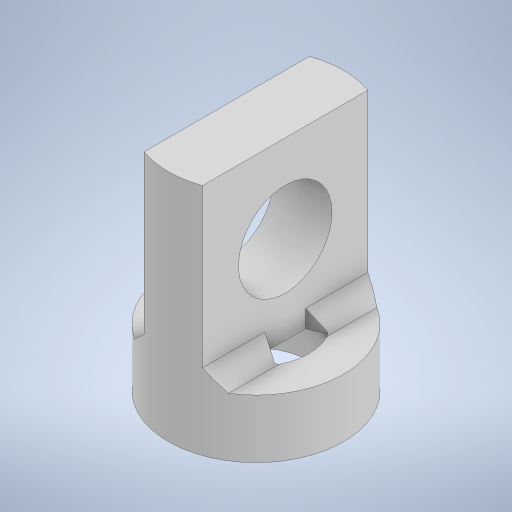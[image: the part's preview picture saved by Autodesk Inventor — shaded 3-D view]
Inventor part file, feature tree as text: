
AUTODESK INVENTOR PART (.ipt)
format: ipt  version: 2024 (Build 280153000, 153)  size: 267,776 bytes
history: native  units: mm
features: extrude x3, sketch x3, chamfer x2, other x1, projected_geometry x1
ambient origin geometry x8: Origin, YZ Plane, XZ Plane, XY Plane, X Axis, Y Axis, Z Axis, Center Point
bodies: Body1 (feature_tree)
feature tree (10):
  other  "솔리드1"
  extrude  "돌출1"  Depth=3.0mm
  extrude  "돌출3"  Depth=1.0mm TaperAngle=0.0deg
  chamfer  "모따기1"  Distance=1.8mm
  chamfer  "모따기2"  Distance=1.0mm
  extrude  "돌출4"  Depth=3.0mm TaperAngle=0.0deg
  sketch  "스케치2"
  sketch  "스케치4"
  sketch  "스케치5"
  projected_geometry  "투영된 루프1"
